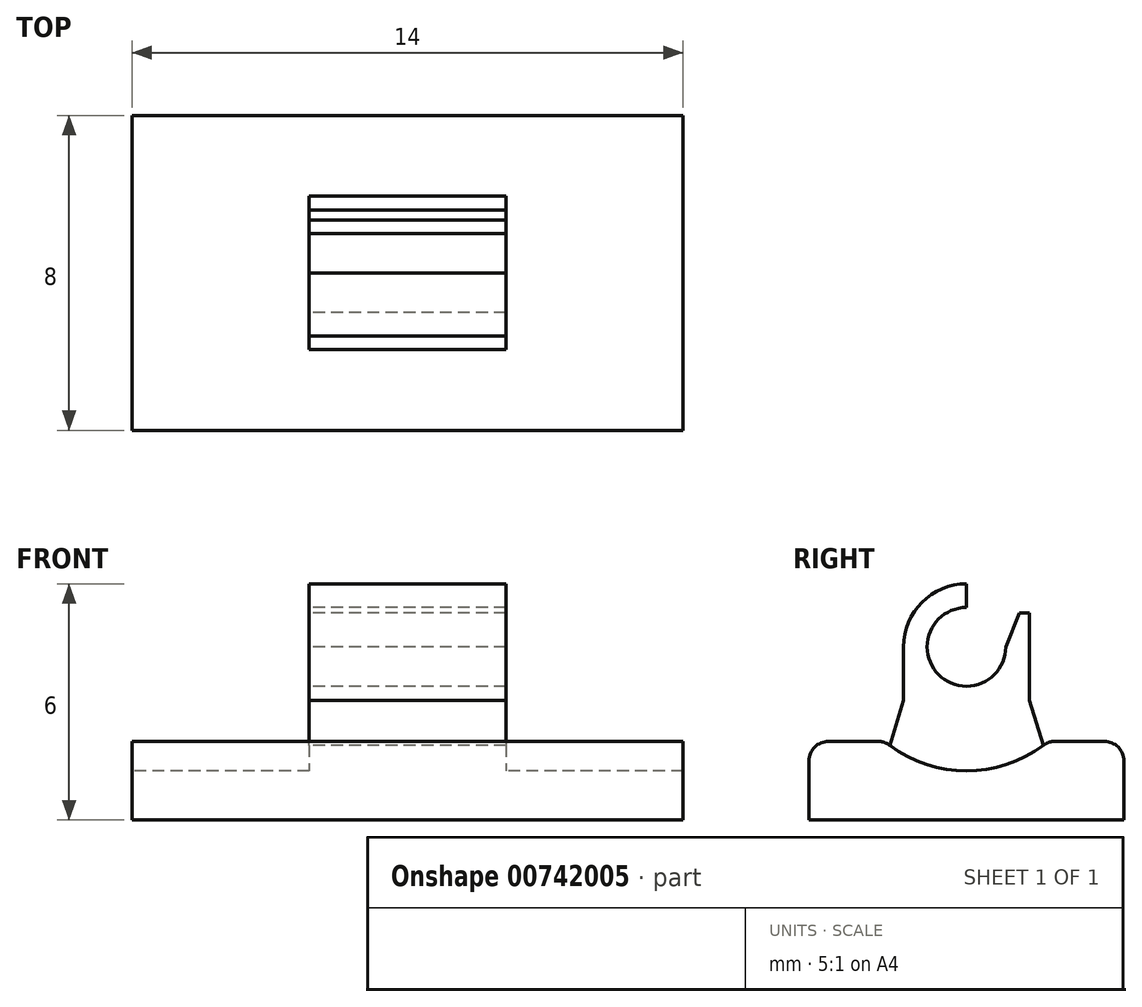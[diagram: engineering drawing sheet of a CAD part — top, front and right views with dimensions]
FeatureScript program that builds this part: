
annotation { "Feature Type Name" : "Feature", "Feature Type Description" : "" }
export const myFeature = defineFeature(function(context is Context, id is Id, definition is map)
    precondition{}
    {
        {
            var Q0;
            Q0=qCreatedBy(makeId("Top.planeOp"),FACE);
            var sketch = newSketch(context, id + "F0", { "sketchPlane" : qUnion([Q0])});
            skLineSegment(sketch, "E0.bottom", {"start": v(7, -4) * mm, "end": v(-7, -4) * mm});
            skLineSegment(sketch, "E0.top", {"start": v(7, 4) * mm, "end": v(-7, 4) * mm});
            skLineSegment(sketch, "E0.left", {"start": v(7, -4) * mm, "end": v(7, 4) * mm});
            skLineSegment(sketch, "E0.right", {"start": v(-7, -4) * mm, "end": v(-7, 4) * mm});
            skPoint(sketch, "E0.middle", {"position": v(0, 0) * mm});
            skSolve(sketch);
        }
        {
            var Q0;
            Q0=makeQuery(id+"F0.imprint","IMPRINT",FACE,{"disambiguationData":[TD([[makeQuery(id+"F0.imprint","IMPRINT",EDGE,{"derivedFrom":sQuery(id+"F0.wireOp",EDGE,"E0.bottom")}),-1.0]])]});
            extrude(context, id + "F1", {"entities" : qUnion([Q0]), "depth" : 6 * mm, "offsetDistance" : 25 * mm});
        }
        {
            var Q0;
            Q0=makeQuery(id+"F1.opExtrude","SWEPT_FACE",FACE,{"disambiguationData":[OSD([sQuery(id+"F0.wireOp",EDGE,"E0.right")])]});
            var sketch = newSketch(context, id + "F2", { "sketchPlane" : qUnion([Q0])});
            skCircle(sketch, "E1", {"center": v(0, 4.5) * mm, "radius": 3.25 * mm});
            skSolve(sketch);
        }
        {
            var Q0;
            {var subQ0=sQuery(id+"F2.wireOp",EDGE,"E1");var subQ1=makeQuery(id+"F1.opExtrude","CAP_EDGE",EDGE,{"disambiguationData":[OSD([sQuery(id+"F0.wireOp",EDGE,"E0.right")])],"isStart":false});var subQ2=makeQuery(id+"F2.imprint","INTERSECT",VERTEX,{"disambiguationData":[OD(0.0)],"derivedFrom":[subQ1,subQ0]});Q0=makeQuery(id+"F2.imprint","IMPRINT",FACE,{"disambiguationData":[TD([[makeQuery(id+"F2.imprint","IMPRINT",EDGE,{"disambiguationData":[TD([[subQ2,-1.0]])],"derivedFrom":subQ0}),1.0]])]});}
            var Q1;
            {var subQ0=sQuery(id+"F2.wireOp",EDGE,"E1");var subQ1=makeQuery(id+"F1.opExtrude","CAP_EDGE",EDGE,{"disambiguationData":[OSD([sQuery(id+"F0.wireOp",EDGE,"E0.right")])],"isStart":false});var subQ2=makeQuery(id+"F2.imprint","INTERSECT",VERTEX,{"disambiguationData":[OD(0.0)],"derivedFrom":[subQ1,subQ0]});Q1=makeQuery(id+"F2.imprint","IMPRINT",FACE,{"disambiguationData":[TD([[makeQuery(id+"F2.imprint","IMPRINT",EDGE,{"disambiguationData":[TD([[subQ2,1.0]])],"derivedFrom":subQ0}),1.0]])]});}
            extrude(context, id + "F3", {"entities" : qUnion([Q0, Q1]), "operationType" : NewBodyOperationType.REMOVE, "endBound" : BoundingType.SYMMETRIC, "oppositeDirection" : true, "depth" : 50 * mm, "offsetDistance" : 25 * mm});
        }
        {
            var Q0;
            Q0=makeQuery(id+"F1.opExtrude","SWEPT_FACE",FACE,{"disambiguationData":[OSD([sQuery(id+"F0.wireOp",EDGE,"E0.right")])]});
            var sketch = newSketch(context, id + "F4", { "sketchPlane" : qUnion([Q0])});
            skLineSegment(sketch, "E2.bottom", {"start": v(8.33, 11.02) * mm, "end": v(-8.33, 11.02) * mm});
            skLineSegment(sketch, "E2.top", {"start": v(8.33, 2) * mm, "end": v(-8.33, 2) * mm});
            skLineSegment(sketch, "E2.left", {"start": v(8.33, 11.02) * mm, "end": v(8.33, 2) * mm});
            skLineSegment(sketch, "E2.right", {"start": v(-8.33, 11.02) * mm, "end": v(-8.33, 2) * mm});
            skPoint(sketch, "E2.middle", {"position": v(0, 6.5) * mm});
            skSolve(sketch);
        }
        {
            var Q0;
            Q0=makeQuery(id+"F4.imprint","IMPRINT",FACE,{"disambiguationData":[TD([[makeQuery(id+"F4.imprint","IMPRINT",EDGE,{"derivedFrom":sQuery(id+"F4.wireOp",EDGE,"E2.bottom")}),1.0]])]});
            var Q1;
            {var subQ0=sQuery(id+"F4.wireOp",EDGE,"E2.top");var subQ1=sQuery(id+"F0.wireOp",EDGE,"E0.right");var subQ2=sQuery(id+"F0.wireOp",EDGE,"E0.top");var subQ3=makeQuery(id+"F1.opExtrude","SWEPT_EDGE",EDGE,{"disambiguationData":[OSD([subQ2,subQ1])]});var subQ4=makeQuery(id+"F4.imprint","INTERSECT",VERTEX,{"derivedFrom":[subQ3,subQ0]});Q1=makeQuery(id+"F4.imprint","IMPRINT",FACE,{"disambiguationData":[TD([[makeQuery(id+"F4.imprint","IMPRINT",EDGE,{"disambiguationData":[TD([[subQ4,1.0]])],"derivedFrom":subQ0}),-1.0]])]});}
            var Q2;
            {var subQ0=sQuery(id+"F4.wireOp",EDGE,"E2.top");var subQ1=sQuery(id+"F0.wireOp",EDGE,"E0.right");var subQ2=sQuery(id+"F0.wireOp",EDGE,"E0.bottom");var subQ3=makeQuery(id+"F1.opExtrude","SWEPT_EDGE",EDGE,{"disambiguationData":[OSD([subQ2,subQ1])]});var subQ4=makeQuery(id+"F4.imprint","INTERSECT",VERTEX,{"derivedFrom":[subQ3,subQ0]});Q2=makeQuery(id+"F4.imprint","IMPRINT",FACE,{"disambiguationData":[TD([[makeQuery(id+"F4.imprint","IMPRINT",EDGE,{"disambiguationData":[TD([[subQ4,-1.0]])],"derivedFrom":subQ0}),-1.0]])]});}
            extrude(context, id + "F5", {"entities" : qUnion([Q0, Q1, Q2]), "operationType" : NewBodyOperationType.REMOVE, "endBound" : BoundingType.SYMMETRIC, "oppositeDirection" : true, "depth" : 30 * mm, "offsetDistance" : 25 * mm});
        }
        {
            var Q0;
            Q0=makeQuery(id+"F5.boolean.opBoolean","INTERSECT",EDGE,{"derivedFrom":[makeQuery(id+"F1.opExtrude","SWEPT_FACE",FACE,{"disambiguationData":[OSD([sQuery(id+"F0.wireOp",EDGE,"E0.top")])]}),makeQuery(id+"F5.opExtrude","SWEPT_FACE",FACE,{"disambiguationData":[OSD([sQuery(id+"F4.wireOp",EDGE,"E2.top")])]})]});
            var Q1;
            Q1=makeQuery(id+"F5.boolean.opBoolean","INTERSECT",EDGE,{"disambiguationData":[OD(1.0)],"derivedFrom":[makeQuery(id+"F3.boolean.opBoolean","COPY",FACE,{"derivedFrom":makeQuery(id+"F3.opExtrude","SWEPT_FACE",FACE,{"disambiguationData":[OSD([sQuery(id+"F2.wireOp",EDGE,"E1")])]})}),makeQuery(id+"F5.opExtrude","SWEPT_FACE",FACE,{"disambiguationData":[OSD([sQuery(id+"F4.wireOp",EDGE,"E2.top")])]})]});
            var Q2;
            Q2=makeQuery(id+"F5.boolean.opBoolean","INTERSECT",EDGE,{"disambiguationData":[OD(0.0)],"derivedFrom":[makeQuery(id+"F3.boolean.opBoolean","COPY",FACE,{"derivedFrom":makeQuery(id+"F3.opExtrude","SWEPT_FACE",FACE,{"disambiguationData":[OSD([sQuery(id+"F2.wireOp",EDGE,"E1")])]})}),makeQuery(id+"F5.opExtrude","SWEPT_FACE",FACE,{"disambiguationData":[OSD([sQuery(id+"F4.wireOp",EDGE,"E2.top")])]})]});
            var Q3;
            Q3=makeQuery(id+"F5.boolean.opBoolean","INTERSECT",EDGE,{"derivedFrom":[makeQuery(id+"F1.opExtrude","SWEPT_FACE",FACE,{"disambiguationData":[OSD([sQuery(id+"F0.wireOp",EDGE,"E0.bottom")])]}),makeQuery(id+"F5.opExtrude","SWEPT_FACE",FACE,{"disambiguationData":[OSD([sQuery(id+"F4.wireOp",EDGE,"E2.top")])]})]});
            fillet(context, id + "F6", {"entities" : qUnion([Q0, Q1, Q2, Q3]), "radius" : 0.5 * mm, "tangentPropagation" : true, "allowEdgeOverflow" : false});
        }
        {
            var Q0;
            Q0=qCreatedBy(makeId("Right.planeOp"),FACE);
            var sketch = newSketch(context, id + "F7", { "sketchPlane" : qUnion([Q0])});
            skLineSegment(sketch, "E3.bottom", {"start": v(-3, -6) * mm, "end": v(3, -6) * mm});
            skLineSegment(sketch, "E3.top", {"start": v(-3, 6) * mm, "end": v(3, 6) * mm});
            skLineSegment(sketch, "E3.left", {"start": v(-3, -6) * mm, "end": v(-3, 6) * mm});
            skLineSegment(sketch, "E3.right", {"start": v(3, -6) * mm, "end": v(3, 6) * mm});
            skPoint(sketch, "E3.middle", {"position": v(0, 0) * mm});
            skLineSegment(sketch, "E4", {"start": v(3, 0) * mm, "end": v(-3, 0) * mm});
            skSolve(sketch);
        }
        {
            var Q0;
            {var subQ0=sQuery(id+"F7.wireOp",EDGE,"E3.top");Q0=makeQuery(id+"F7.imprint","IMPRINT",FACE,{"disambiguationData":[TD([[makeQuery(id+"F7.imprint","IMPRINT",EDGE,{"derivedFrom":subQ0}),-1.0]])]});}
            extrude(context, id + "F8", {"entities" : qUnion([Q0]), "operationType" : NewBodyOperationType.ADD, "endBound" : BoundingType.SYMMETRIC, "depth" : 5 * mm, "offsetDistance" : 25 * mm});
        }
        {
            var Q0;
            Q0=makeQuery(id+"F8.opExtrude","CAP_FACE",FACE,{"disambiguationData":[OSD([sQuery(id+"F7.wireOp",EDGE,"E3.top"),sQuery(id+"F7.wireOp",EDGE,"E3.left"),sQuery(id+"F7.wireOp",EDGE,"E3.right"),sQuery(id+"F7.wireOp",EDGE,"E4")])],"isStart":true});
            var sketch = newSketch(context, id + "F9", { "sketchPlane" : qUnion([Q0])});
            skArc(sketch, "E5", {"start": v(-1, 4.4) * mm, "mid": v(0.7, 3.7) * mm, "end": v(0, 5.4) * mm});
            skLineSegment(sketch, "E6", {"start": v(-1.6, 4.4) * mm, "end": v(-1.6, 3.04) * mm});
            skLineSegment(sketch, "E7", {"start": v(0, 4.4) * mm, "end": v(1.6, 4.4) * mm});
            skLineSegment(sketch, "E8", {"start": v(1.6, 4.4) * mm, "end": v(1.6, 3.04) * mm});
            skLineSegment(sketch, "E9", {"start": v(0, 5.4) * mm, "end": v(0, 6) * mm});
            skLineSegment(sketch, "E10", {"start": v(-1, 4.4) * mm, "end": v(-1.34, 5.27) * mm});
            skLineSegment(sketch, "E11", {"start": v(-1.34, 5.27) * mm, "end": v(-1.6, 5.27) * mm});
            skLineSegment(sketch, "E12", {"start": v(-1.6, 5.27) * mm, "end": v(-1.6, 4.4) * mm});
            skArc(sketch, "E13.trimOffspring", {"start": v(1.6, 4.4) * mm, "mid": v(1.13, 5.53) * mm, "end": v(0, 6) * mm});
            skLineSegment(sketch, "E14", {"start": v(1.95, 1.9) * mm, "end": v(1.6, 3.04) * mm});
            skLineSegment(sketch, "E15.MirrorCS", {"start": v(-1.95, 1.9) * mm, "end": v(-1.6, 3.04) * mm});
            skPoint(sketch, "E16.orphan", {"position": v(1.6, 1.67) * mm});
            skSolve(sketch);
        }
        {
            var Q0;
            Q0=makeQuery(id+"F9.imprint","IMPRINT",FACE,{"disambiguationData":[TD([[makeQuery(id+"F9.imprint","IMPRINT",EDGE,{"derivedFrom":sQuery(id+"F9.wireOp",EDGE,"E6")}),-1.0]])]});
            var Q1;
            Q1=makeQuery(id+"F9.imprint","IMPRINT",FACE,{"disambiguationData":[TD([[makeQuery(id+"F9.imprint","IMPRINT",EDGE,{"derivedFrom":sQuery(id+"F9.wireOp",EDGE,"E8")}),1.0]])]});
            extrude(context, id + "F10", {"entities" : qUnion([Q0, Q1]), "operationType" : NewBodyOperationType.REMOVE, "oppositeDirection" : true, "depth" : 25 * mm, "offsetDistance" : 25 * mm});
        }
    });
